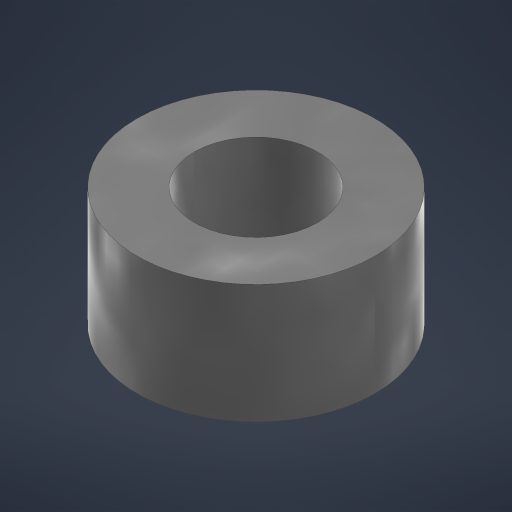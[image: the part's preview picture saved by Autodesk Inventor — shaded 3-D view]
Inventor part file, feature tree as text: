
AUTODESK INVENTOR PART (.ipt)
format: ipt  version: 2024 (Build 280153000, 153)  size: 190,464 bytes
history: native  units: in
note: dims shown in document units (in); Inventor stores cm internally (conversion verified against a paired STEP export)
features: extrude x1, sketch x1
ambient origin geometry x8: Origin, YZ Plane, XZ Plane, XY Plane, X Axis, Y Axis, Z Axis, Center Point
bodies: Solid1 (feature_tree)
feature tree (2):
  extrude  "Extrusion1"  Depth=0.1181in
  sketch  "Sketch1"  dims[d0=0.122in d1=0.2362in d2=0.1181in d3=0.0in]
